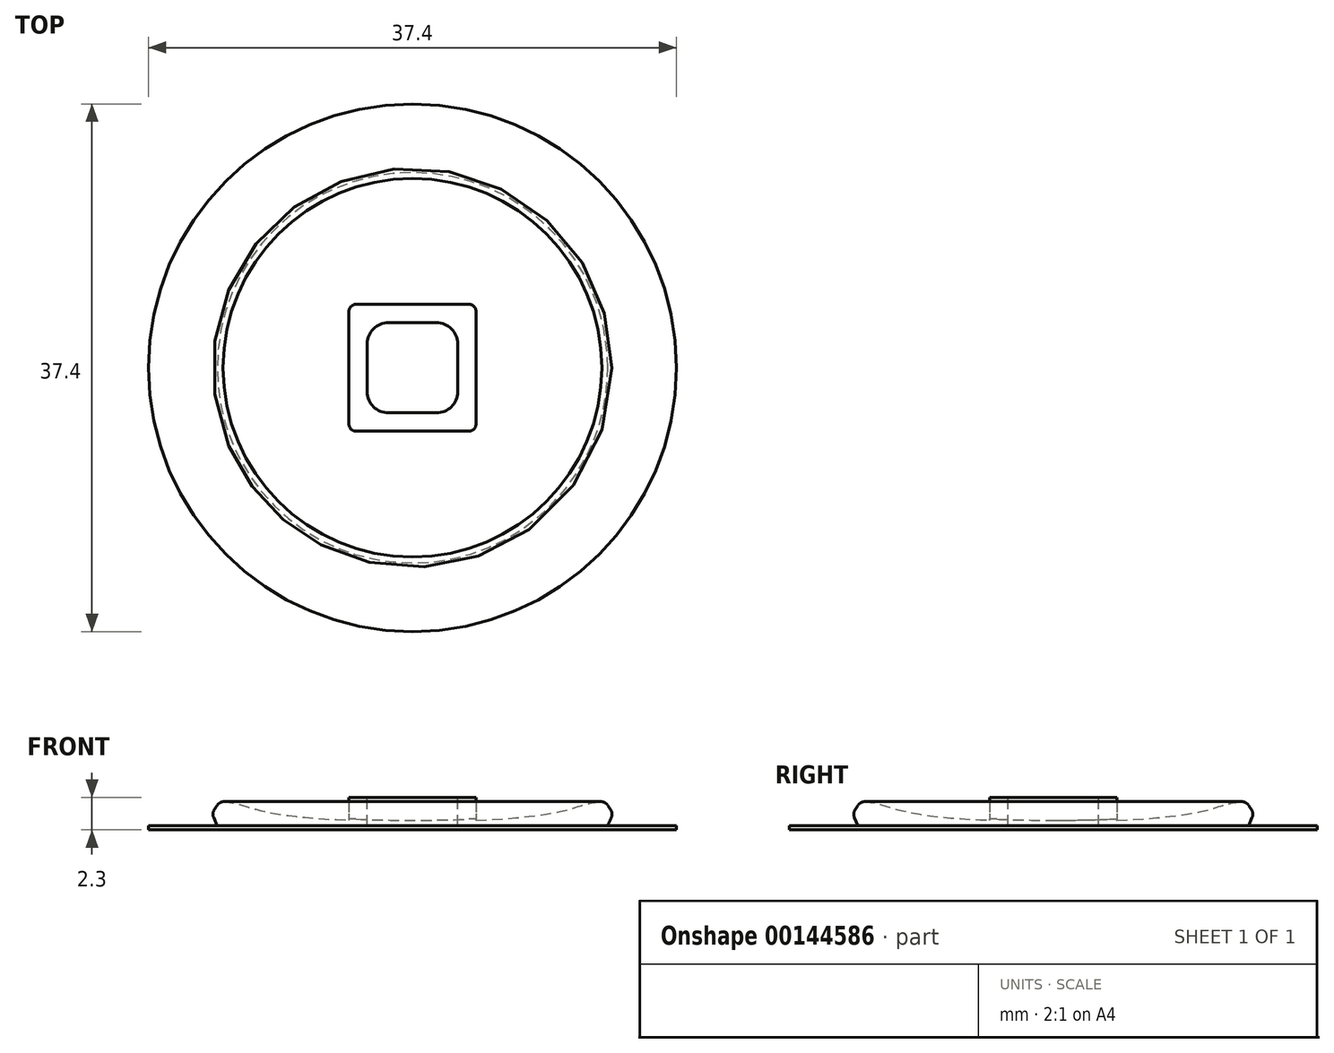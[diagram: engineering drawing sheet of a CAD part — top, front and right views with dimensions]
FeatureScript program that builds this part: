
annotation { "Feature Type Name" : "Feature", "Feature Type Description" : "" }
export const myFeature = defineFeature(function(context is Context, id is Id, definition is map)
    precondition{}
    {
        {
            var Q0;
            Q0=qCreatedBy(makeId("Top.planeOp"),FACE);
            var sketch = newSketch(context, id + "F0", { "sketchPlane" : qUnion([Q0])});
            skCircle(sketch, "E0", {"center": v(0, 0) * mm, "radius": 13.7 * mm});
            skCircle(sketch, "E1.0", {"center": v(0, 0) * mm, "radius": 18.7 * mm});
            skCircle(sketch, "E2", {"center": v(0, 0) * mm, "radius": 14.15 * mm, "construction": true});
            skSolve(sketch);
        }
        {
            var Q0;
            Q0 = qSketchRegion(id + "F0", true);
            var Q1;
            Q1=makeQuery(id+"F0.imprint","IMPRINT",FACE,{"disambiguationData":[TD([[makeQuery(id+"F0.imprint","IMPRINT",EDGE,{"derivedFrom":sQuery(id+"F0.wireOp",EDGE,"E0")}),1.0]])]});
            extrude(context, id + "F1", {"entities" : qUnion([Q0, Q1]), "depth" : .3 * mm});
        }
        {
            var Q0;
            Q0=makeQuery(id+"F0.imprint","IMPRINT",FACE,{"disambiguationData":[TD([[makeQuery(id+"F0.imprint","IMPRINT",EDGE,{"derivedFrom":sQuery(id+"F0.wireOp",EDGE,"E0")}),1.0]])]});
            extrude(context, id + "F2", {"entities" : qUnion([Q0]), "operationType" : NewBodyOperationType.ADD, "depth" : 2 * mm, "hasDraft" : true, "draftAngle" : 24 * degree});
        }
        {
            var Q0;
            Q0=makeQuery(id+"F2.opExtrude","CAP_EDGE",EDGE,{"disambiguationData":[OSD([sQuery(id+"F0.wireOp",EDGE,"E0")])],"isStart":false});
            chamfer(context, id + "F3", {"entities" : qUnion([Q0]), "width" : 0.6 * mm, "tangentPropagation" : true});
        }
        {
            var Q0;
            {var subQ0=sQuery(id+"F0.wireOp",EDGE,"E0");Q0=makeQuery(id+"F3.opChamfer","BLEND_EDGE",EDGE,{"blendedFrom":[makeQuery(id+"F2.opExtrude","CAP_EDGE",EDGE,{"disambiguationData":[OSD([subQ0])],"isStart":false}),makeQuery(id+"F2.opExtrude","SWEPT_FACE",FACE,{"disambiguationData":[OSD([subQ0])]})],"blendedInto":[makeQuery(id+"F2.opExtrude","SWEPT_FACE",FACE,{"disambiguationData":[OSD([subQ0])]})]});}
            var Q1;
            {var subQ0=sQuery(id+"F0.wireOp",EDGE,"E0");Q1=makeQuery(id+"F3.opChamfer","BLEND_EDGE",EDGE,{"blendedFrom":[makeQuery(id+"F2.opExtrude","CAP_EDGE",EDGE,{"disambiguationData":[OSD([subQ0])],"isStart":false}),makeQuery(id+"F2.opExtrude","CAP_FACE",FACE,{"disambiguationData":[OSD([subQ0])],"isStart":false})],"blendedInto":[makeQuery(id+"F2.opExtrude","CAP_FACE",FACE,{"disambiguationData":[OSD([subQ0])],"isStart":false})]});}
            fillet(context, id + "F4", {"entities" : qUnion([Q0, Q1]), "radius" : 0.6 * mm, "tangentPropagation" : true, "allowEdgeOverflow" : false});
        }
        {
            var Q0;
            Q0=qCreatedBy(makeId("Front.planeOp"),FACE);
            var sketch = newSketch(context, id + "F5", { "sketchPlane" : qUnion([Q0])});
            skLineSegment(sketch, "E3.0", {"start": v(-13.66, 2) * mm, "end": v(13.66, 2) * mm, "construction": true});
            skLineSegment(sketch, "E4.0", {"start": v(13.83, 0.3) * mm, "end": v(-13.83, 0.3) * mm, "construction": true});
            skFitSpline(sketch, "E5", {"points": [v(-13.66, 2) * mm, v(0, 0.6) * mm], "startDerivative": vector(7.6, 0) * mm, "endDerivative": vector(36.7, 0) * mm});
            skLineSegment(sketch, "E6", {"start": v(0, 2) * mm, "end": v(0, 0.6) * mm});
            skLineSegment(sketch, "E7", {"start": v(0, 2) * mm, "end": v(-13.66, 2) * mm});
            skSolve(sketch);
        }
        {
            var Q0;
            Q0=makeQuery(id+"F5.imprint","IMPRINT",FACE,{"disambiguationData":[TD([[makeQuery(id+"F5.imprint","IMPRINT",EDGE,{"derivedFrom":sQuery(id+"F5.wireOp",EDGE,"E5")}),1.0]])]});
            var Q1;
            Q1=sQuery(id+"F5.wireOp",EDGE,"E6");
            revolve(context, id + "F6", {"entities" : qUnion([Q0]), "axis" : qUnion([Q1]), "revolveType" : RevolveType.FULL, "oppositeDirection" : true});
        }
        {
            var Q0;
            Q0=makeQuery(id+"F6.opRevolve","SWEPT_BODY",BODY,{"disambiguationData":[OSD([sQuery(id+"F5.wireOp",EDGE,"E5"),sQuery(id+"F5.wireOp",EDGE,"E6"),sQuery(id+"F5.wireOp",EDGE,"E7")])]});
            var Q1;
            Q1=makeQuery(id+"F1.opExtrude","SWEPT_BODY",BODY,{"disambiguationData":[OSD([sQuery(id+"F0.wireOp",EDGE,"E1.0")])]});
            booleanBodies(context, id + "F7", {"operationType" : BooleanOperationType.SUBTRACTION, "tools" : qUnion([Q0]), "targets" : qUnion([Q1])});
        }
        {
            var Q0;
            Q0=makeQuery(id+"F1.opExtrude","CAP_FACE",FACE,{"disambiguationData":[OSD([sQuery(id+"F0.wireOp",EDGE,"E1.0")])],"isStart":false});
            var sketch = newSketch(context, id + "F8", { "sketchPlane" : qUnion([Q0])});
            skLineSegment(sketch, "E8.bottom", {"start": v(4.5, 4.5) * mm, "end": v(-4.5, 4.5) * mm});
            skLineSegment(sketch, "E8.top", {"start": v(4.5, -4.5) * mm, "end": v(-4.5, -4.5) * mm});
            skLineSegment(sketch, "E8.left", {"start": v(4.5, 4.5) * mm, "end": v(4.5, -4.5) * mm});
            skLineSegment(sketch, "E8.right", {"start": v(-4.5, 4.5) * mm, "end": v(-4.5, -4.5) * mm});
            skPoint(sketch, "E8.middle", {"position": v(0, 0) * mm});
            skSolve(sketch);
        }
        {
            var Q0;
            Q0 = qSketchRegion(id + "F8", true);
            extrude(context, id + "F9", {"entities" : qUnion([Q0]), "operationType" : NewBodyOperationType.ADD, "depth" : 2 * mm});
        }
        {
            var Q0;
            Q0=makeQuery(id+"F9.opExtrude","SWEPT_EDGE",EDGE,{"disambiguationData":[OSD([sQuery(id+"F8.wireOp",EDGE,"E8.bottom"),sQuery(id+"F8.wireOp",EDGE,"E8.right")])]});
            var Q1;
            Q1=makeQuery(id+"F9.opExtrude","SWEPT_EDGE",EDGE,{"disambiguationData":[OSD([sQuery(id+"F8.wireOp",EDGE,"E8.top"),sQuery(id+"F8.wireOp",EDGE,"E8.right")])]});
            var Q2;
            Q2=makeQuery(id+"F9.opExtrude","SWEPT_EDGE",EDGE,{"disambiguationData":[OSD([sQuery(id+"F8.wireOp",EDGE,"E8.top"),sQuery(id+"F8.wireOp",EDGE,"E8.left")])]});
            var Q3;
            Q3=makeQuery(id+"F9.opExtrude","SWEPT_EDGE",EDGE,{"disambiguationData":[OSD([sQuery(id+"F8.wireOp",EDGE,"E8.bottom"),sQuery(id+"F8.wireOp",EDGE,"E8.left")])]});
            fillet(context, id + "F10", {"entities" : qUnion([Q0, Q1, Q2, Q3]), "radius" : .5 * mm, "tangentPropagation" : true, "allowEdgeOverflow" : false});
        }
        {
            var Q0;
            Q0=makeQuery(id+"F9.opExtrude","CAP_FACE",FACE,{"disambiguationData":[OSD([sQuery(id+"F8.wireOp",EDGE,"E8.bottom"),sQuery(id+"F8.wireOp",EDGE,"E8.top"),sQuery(id+"F8.wireOp",EDGE,"E8.left"),sQuery(id+"F8.wireOp",EDGE,"E8.right")])],"isStart":false});
            var sketch = newSketch(context, id + "F11", { "sketchPlane" : qUnion([Q0])});
            skLineSegment(sketch, "E9.0", {"start": v(3.2, -3.2) * mm, "end": v(3.2, 3.2) * mm});
            skLineSegment(sketch, "E9.1", {"start": v(-3.2, -3.2) * mm, "end": v(3.2, -3.2) * mm});
            skLineSegment(sketch, "E9.2", {"start": v(-3.2, 3.2) * mm, "end": v(-3.2, -3.2) * mm});
            skLineSegment(sketch, "E9.3", {"start": v(3.2, 3.2) * mm, "end": v(-3.2, 3.2) * mm});
            skSolve(sketch);
        }
        {
            var Q0;
            Q0=makeQuery(id+"F11.imprint","IMPRINT",FACE,{"disambiguationData":[TD([[makeQuery(id+"F11.imprint","IMPRINT",EDGE,{"derivedFrom":sQuery(id+"F11.wireOp",EDGE,"E9.0")}),1.0]])]});
            var Q1;
            Q1=makeQuery(id+"F1.opExtrude","CAP_FACE",FACE,{"disambiguationData":[OSD([sQuery(id+"F0.wireOp",EDGE,"E1.0")])],"isStart":false});
            extrude(context, id + "F12", {"entities" : qUnion([Q0]), "operationType" : NewBodyOperationType.REMOVE, "endBound" : BoundingType.UP_TO_SURFACE, "oppositeDirection" : true, "endBoundEntityFace" : qUnion([Q1]), "depth" : 25 * mm});
        }
        {
            var Q0;
            Q0=makeQuery(id+"F12.boolean.opBoolean","COPY",EDGE,{"derivedFrom":makeQuery(id+"F12.opExtrude","SWEPT_EDGE",EDGE,{"disambiguationData":[OSD([sQuery(id+"F11.wireOp",EDGE,"E9.2"),sQuery(id+"F11.wireOp",EDGE,"E9.3")])]})});
            var Q1;
            Q1=makeQuery(id+"F12.boolean.opBoolean","COPY",EDGE,{"derivedFrom":makeQuery(id+"F12.opExtrude","SWEPT_EDGE",EDGE,{"disambiguationData":[OSD([sQuery(id+"F11.wireOp",EDGE,"E9.0"),sQuery(id+"F11.wireOp",EDGE,"E9.3")])]})});
            var Q2;
            Q2=makeQuery(id+"F12.boolean.opBoolean","COPY",EDGE,{"derivedFrom":makeQuery(id+"F12.opExtrude","SWEPT_EDGE",EDGE,{"disambiguationData":[OSD([sQuery(id+"F11.wireOp",EDGE,"E9.0"),sQuery(id+"F11.wireOp",EDGE,"E9.1")])]})});
            var Q3;
            Q3=makeQuery(id+"F12.boolean.opBoolean","COPY",EDGE,{"derivedFrom":makeQuery(id+"F12.opExtrude","SWEPT_EDGE",EDGE,{"disambiguationData":[OSD([sQuery(id+"F11.wireOp",EDGE,"E9.1"),sQuery(id+"F11.wireOp",EDGE,"E9.2")])]})});
            var Q4;
            Q4=makeQuery(id+"F12.boolean.opBoolean","COPY",FACE,{"derivedFrom":makeQuery(id+"F12.opExtrude","CAP_FACE",FACE,{"disambiguationData":[OSD([sQuery(id+"F0.wireOp",EDGE,"E1.0")])],"isStart":false})});
            fillet(context, id + "F13", {"entities" : qUnion([Q0, Q1, Q2, Q3, Q4]), "radius" : 1.5 * mm, "tangentPropagation" : true, "allowEdgeOverflow" : false});
        }
    });
